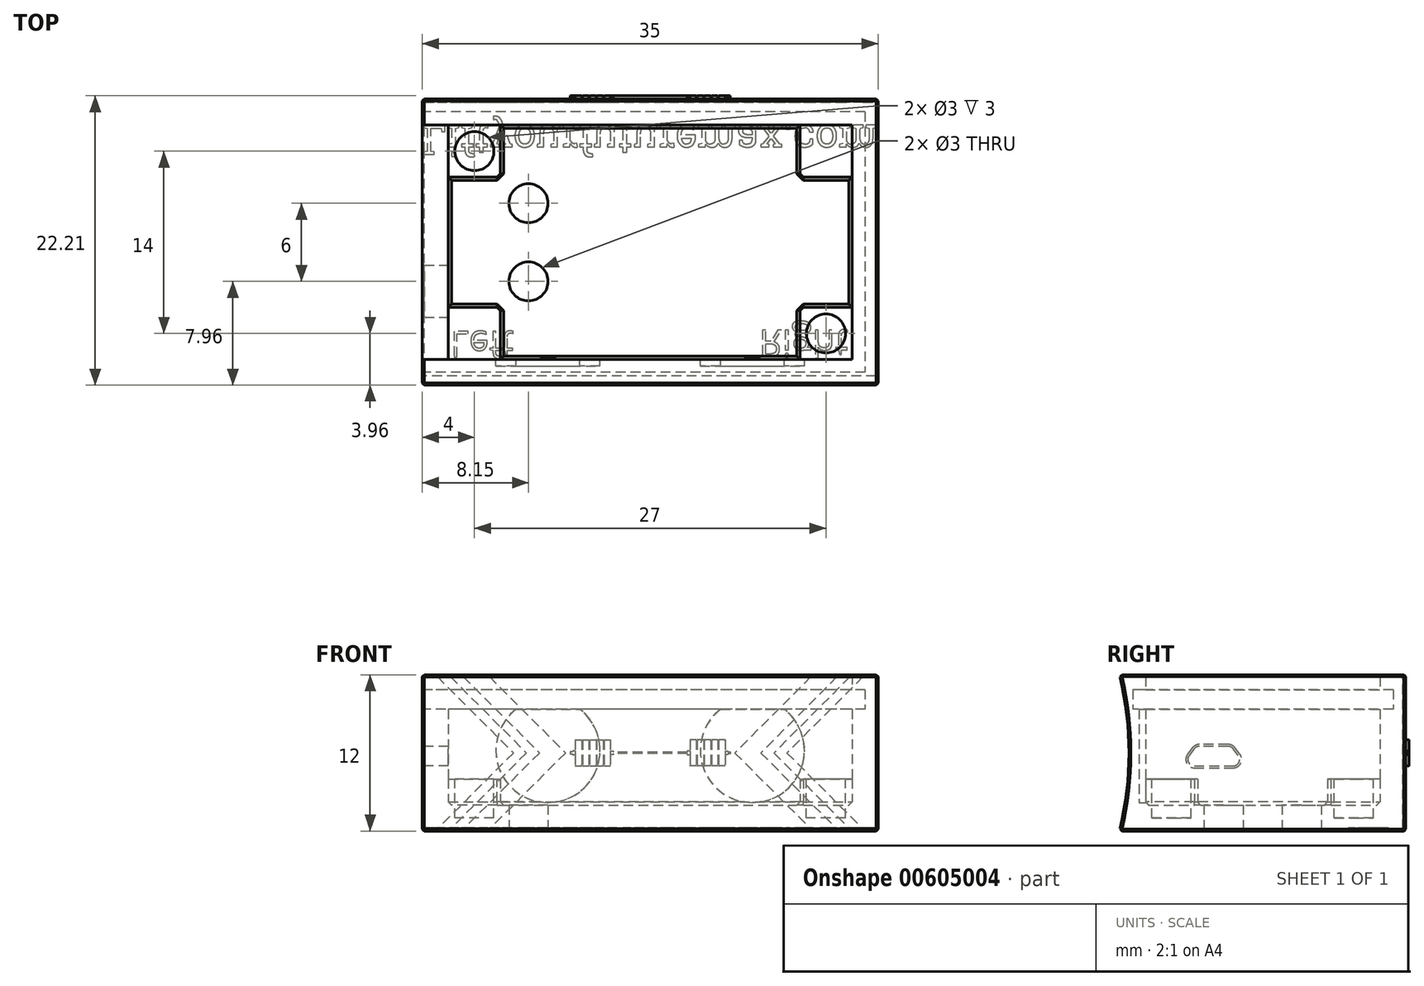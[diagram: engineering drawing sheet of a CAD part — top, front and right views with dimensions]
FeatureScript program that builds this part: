
annotation { "Feature Type Name" : "Feature", "Feature Type Description" : "" }
export const myFeature = defineFeature(function(context is Context, id is Id, definition is map)
    precondition{}
    {
        {
            var Q0;
            Q0=qCreatedBy(makeId("Top.planeOp"),FACE);
            var sketch = newSketch(context, id + "F0", { "sketchPlane" : qUnion([Q0])});
            skLineSegment(sketch, "E0.bottom", {"start": v(-17.5, 11) * mm, "end": v(17.5, 11) * mm});
            skLineSegment(sketch, "E0.top", {"start": v(-17.5, -11) * mm, "end": v(17.5, -11) * mm});
            skLineSegment(sketch, "E0.left", {"start": v(-17.5, 11) * mm, "end": v(-17.5, -11) * mm});
            skLineSegment(sketch, "E0.right", {"start": v(17.5, 11) * mm, "end": v(17.5, -11) * mm});
            skSolve(sketch);
        }
        {
            var Q0;
            Q0 = qSketchRegion(id + "F0", true);
            extrude(context, id + "F1", {"entities" : qUnion([Q0]), "depth" : 12 * mm, "offsetDistance" : 25 * mm});
        }
        {
            var Q0;
            Q0=makeQuery(id+"F1.opExtrude","CAP_FACE",FACE,{"disambiguationData":[OSD([sQuery(id+"F0.wireOp",EDGE,"E0.bottom"),sQuery(id+"F0.wireOp",EDGE,"E0.top"),sQuery(id+"F0.wireOp",EDGE,"E0.left"),sQuery(id+"F0.wireOp",EDGE,"E0.right")])],"isStart":false});
            shell(context, id + "F2", {"entities" : qUnion([Q0]), "thickness" : 2 * mm});
        }
        {
            var Q0;
            Q0=makeQuery(id+"F2.opShell","OFFSET_FACE",FACE,{"disambiguationData":[OSD([sQuery(id+"F0.wireOp",EDGE,"E0.bottom"),sQuery(id+"F0.wireOp",EDGE,"E0.top"),sQuery(id+"F0.wireOp",EDGE,"E0.left"),sQuery(id+"F0.wireOp",EDGE,"E0.right")])]});
            var sketch = newSketch(context, id + "F3", { "sketchPlane" : qUnion([Q0])});
            skLineSegment(sketch, "E1.bottom", {"start": v(-15.5, 9) * mm, "end": v(-11.5, 9) * mm});
            skLineSegment(sketch, "E1.top", {"start": v(-15.5, 5) * mm, "end": v(-11.5, 5) * mm});
            skLineSegment(sketch, "E1.left", {"start": v(-15.5, 9) * mm, "end": v(-15.5, 5) * mm});
            skLineSegment(sketch, "E1.right", {"start": v(-11.5, 9) * mm, "end": v(-11.5, 5) * mm});
            skLineSegment(sketch, "E2.bottom", {"start": v(15.5, 9) * mm, "end": v(11.5, 9) * mm});
            skLineSegment(sketch, "E2.top", {"start": v(15.5, 5) * mm, "end": v(11.5, 5) * mm});
            skLineSegment(sketch, "E2.left", {"start": v(15.5, 9) * mm, "end": v(15.5, 5) * mm});
            skLineSegment(sketch, "E2.right", {"start": v(11.5, 9) * mm, "end": v(11.5, 5) * mm});
            skLineSegment(sketch, "E3.bottom", {"start": v(15.5, -9) * mm, "end": v(11.5, -9) * mm});
            skLineSegment(sketch, "E3.top", {"start": v(15.5, -5) * mm, "end": v(11.5, -5) * mm});
            skLineSegment(sketch, "E3.left", {"start": v(15.5, -9) * mm, "end": v(15.5, -5) * mm});
            skLineSegment(sketch, "E3.right", {"start": v(11.5, -9) * mm, "end": v(11.5, -5) * mm});
            skLineSegment(sketch, "E4.bottom", {"start": v(-15.5, -9) * mm, "end": v(-11.5, -9) * mm});
            skLineSegment(sketch, "E4.top", {"start": v(-15.5, -5) * mm, "end": v(-11.5, -5) * mm});
            skLineSegment(sketch, "E4.left", {"start": v(-15.5, -9) * mm, "end": v(-15.5, -5) * mm});
            skLineSegment(sketch, "E4.right", {"start": v(-11.5, -9) * mm, "end": v(-11.5, -5) * mm});
            skSolve(sketch);
        }
        {
            var Q0;
            Q0 = qSketchRegion(id + "F3", true);
            extrude(context, id + "F4", {"entities" : qUnion([Q0]), "operationType" : NewBodyOperationType.ADD, "depth" : 2 * mm, "offsetDistance" : 25 * mm});
        }
        {
            var Q0;
            Q0=makeQuery(id+"F4.opExtrude","SWEPT_EDGE",EDGE,{"disambiguationData":[OSD([sQuery(id+"F3.wireOp",EDGE,"E1.top"),sQuery(id+"F3.wireOp",EDGE,"E1.right")])]});
            var Q1;
            {var subQ0=sQuery(id+"F0.wireOp",EDGE,"E0.bottom");Q1=makeQuery(id+"F2.opShell","OFFSET_EDGE",EDGE,{"disambiguationData":[OSD([subQ0]),TDD([makeQuery(id+"F1.opExtrude","CAP_EDGE",EDGE,{"disambiguationData":[OSD([subQ0])],"isStart":true})])]});}
            var Q2;
            {var subQ0=sQuery(id+"F0.wireOp",EDGE,"E0.left");Q2=makeQuery(id+"F2.opShell","OFFSET_EDGE",EDGE,{"disambiguationData":[OSD([subQ0]),TDD([makeQuery(id+"F1.opExtrude","CAP_EDGE",EDGE,{"disambiguationData":[OSD([subQ0])],"isStart":true})])]});}
            var Q3;
            Q3=makeQuery(id+"F2.opShell","OFFSET_FACE",FACE,{"disambiguationData":[OSD([sQuery(id+"F0.wireOp",EDGE,"E0.bottom"),sQuery(id+"F0.wireOp",EDGE,"E0.top"),sQuery(id+"F0.wireOp",EDGE,"E0.left"),sQuery(id+"F0.wireOp",EDGE,"E0.right")])]});
            var Q4;
            Q4=makeQuery(id+"F4.opExtrude","SWEPT_EDGE",EDGE,{"disambiguationData":[OSD([sQuery(id+"F3.wireOp",EDGE,"E2.top"),sQuery(id+"F3.wireOp",EDGE,"E2.right")])]});
            var Q5;
            Q5=makeQuery(id+"F4.opExtrude","SWEPT_EDGE",EDGE,{"disambiguationData":[OSD([sQuery(id+"F3.wireOp",EDGE,"E3.top"),sQuery(id+"F3.wireOp",EDGE,"E3.right")])]});
            var Q6;
            Q6=makeQuery(id+"F4.opExtrude","SWEPT_EDGE",EDGE,{"disambiguationData":[OSD([sQuery(id+"F3.wireOp",EDGE,"E4.top"),sQuery(id+"F3.wireOp",EDGE,"E4.right")])]});
            chamfer(context, id + "F5", {"entities" : qUnion([Q0, Q1, Q2, Q3, Q4, Q5, Q6]), "width" : 0.25 * mm, "tangentPropagation" : true});
        }
        {
            var Q0;
            Q0=makeQuery(id+"F4.opExtrude","CAP_FACE",FACE,{"disambiguationData":[OSD([sQuery(id+"F3.wireOp",EDGE,"E1.bottom"),sQuery(id+"F3.wireOp",EDGE,"E1.top"),sQuery(id+"F3.wireOp",EDGE,"E1.left"),sQuery(id+"F3.wireOp",EDGE,"E1.right")])],"isStart":false});
            var sketch = newSketch(context, id + "F6", { "sketchPlane" : qUnion([Q0])});
            skCircle(sketch, "E5", {"center": v(-13.5, 7) * mm, "radius": 1.5 * mm});
            skPoint(sketch, "E5.centerSnap0", {"position": v(-13.5, 5.88) * mm});
            skPoint(sketch, "E5.centerSnap1", {"position": v(-12.5, 7) * mm});
            skCircle(sketch, "E6.MirrorC", {"center": v(13.5, 7) * mm, "radius": 1.5 * mm});
            skCircle(sketch, "E7.MirrorC", {"center": v(-13.5, -7) * mm, "radius": 1.5 * mm});
            skCircle(sketch, "E8.MirrorC", {"center": v(13.5, -7) * mm, "radius": 1.5 * mm});
            skSolve(sketch);
        }
        {
            var Q0;
            Q0=makeQuery(id+"F6.imprint","IMPRINT",FACE,{"disambiguationData":[TD([[makeQuery(id+"F6.imprint","IMPRINT",EDGE,{"derivedFrom":sQuery(id+"F6.wireOp",EDGE,"E5")}),1.0]])]});
            var Q1;
            Q1=makeQuery(id+"F6.imprint","IMPRINT",FACE,{"disambiguationData":[TD([[makeQuery(id+"F6.imprint","IMPRINT",EDGE,{"derivedFrom":sQuery(id+"F6.wireOp",EDGE,"E6.MirrorC")}),-1.0]])]});
            var Q2;
            Q2=makeQuery(id+"F6.imprint","IMPRINT",FACE,{"disambiguationData":[TD([[makeQuery(id+"F6.imprint","IMPRINT",EDGE,{"derivedFrom":sQuery(id+"F6.wireOp",EDGE,"E8.MirrorC")}),1.0]])]});
            var Q3;
            Q3=makeQuery(id+"F6.imprint","IMPRINT",FACE,{"disambiguationData":[TD([[makeQuery(id+"F6.imprint","IMPRINT",EDGE,{"derivedFrom":sQuery(id+"F6.wireOp",EDGE,"E7.MirrorC")}),-1.0]])]});
            extrude(context, id + "F7", {"entities" : qUnion([Q0, Q1, Q2, Q3]), "operationType" : NewBodyOperationType.REMOVE, "oppositeDirection" : true, "depth" : 3 * mm, "offsetDistance" : 25 * mm});
        }
        {
            var Q0;
            Q0=makeQuery(id+"F1.opExtrude","SWEPT_FACE",FACE,{"disambiguationData":[OSD([sQuery(id+"F0.wireOp",EDGE,"E0.left")])]});
            var sketch = newSketch(context, id + "F8", { "sketchPlane" : qUnion([Q0])});
            skLineSegment(sketch, "E9", {"start": v(1.25, 5) * mm, "end": v(6.25, 5) * mm});
            skLineSegment(sketch, "E10", {"start": v(6.25, 5) * mm, "end": v(5.12, 6.5) * mm});
            skLineSegment(sketch, "E11", {"start": v(5.12, 6.5) * mm, "end": v(2.4, 6.5) * mm});
            skLineSegment(sketch, "E12", {"start": v(2.4, 6.5) * mm, "end": v(1.25, 5) * mm});
            skSolve(sketch);
        }
        {
            var Q0;
            Q0 = qSketchRegion(id + "F8", true);
            extrude(context, id + "F9", {"entities" : qUnion([Q0]), "operationType" : NewBodyOperationType.REMOVE, "oppositeDirection" : true, "depth" : 5 * mm, "offsetDistance" : 25 * mm});
        }
        {
            var Q0;
            Q0=makeQuery(id+"F9.boolean.opBoolean","COPY",EDGE,{"derivedFrom":makeQuery(id+"F9.opExtrude","SWEPT_EDGE",EDGE,{"disambiguationData":[OSD([sQuery(id+"F8.wireOp",EDGE,"E9"),sQuery(id+"F8.wireOp",EDGE,"E10")])]})});
            var Q1;
            Q1=makeQuery(id+"F9.boolean.opBoolean","COPY",EDGE,{"derivedFrom":makeQuery(id+"F9.opExtrude","SWEPT_EDGE",EDGE,{"disambiguationData":[OSD([sQuery(id+"F8.wireOp",EDGE,"E9"),sQuery(id+"F8.wireOp",EDGE,"E12")])]})});
            var Q2;
            Q2=makeQuery(id+"F9.boolean.opBoolean","COPY",EDGE,{"derivedFrom":makeQuery(id+"F9.opExtrude","SWEPT_EDGE",EDGE,{"disambiguationData":[OSD([sQuery(id+"F8.wireOp",EDGE,"E10"),sQuery(id+"F8.wireOp",EDGE,"E11")])]})});
            var Q3;
            Q3=makeQuery(id+"F9.boolean.opBoolean","COPY",EDGE,{"derivedFrom":makeQuery(id+"F9.opExtrude","SWEPT_EDGE",EDGE,{"disambiguationData":[OSD([sQuery(id+"F8.wireOp",EDGE,"E11"),sQuery(id+"F8.wireOp",EDGE,"E12")])]})});
            fillet(context, id + "F10", {"entities" : qUnion([Q0, Q1, Q2, Q3]), "radius" : 0.5 * mm, "tangentPropagation" : true, "allowEdgeOverflow" : false});
        }
        {
            var Q0;
            Q0=makeQuery(id+"F1.opExtrude","CAP_FACE",FACE,{"disambiguationData":[OSD([sQuery(id+"F0.wireOp",EDGE,"E0.bottom"),sQuery(id+"F0.wireOp",EDGE,"E0.top"),sQuery(id+"F0.wireOp",EDGE,"E0.left"),sQuery(id+"F0.wireOp",EDGE,"E0.right")])],"isStart":true});
            var sketch = newSketch(context, id + "F11", { "sketchPlane" : qUnion([Q0])});
            skText(sketch, "E13", { "text": "Liftyourfuturemax.com", "fontName": "RobotoSlab-Regular.ttf"});
            const initialGuessF11  = {"E13": [-0.0175, -0.009, 1, 0, 0.00228]};
            skSetInitialGuess(sketch, initialGuessF11);
            skSolve(sketch);
        }
        {
            var Q0;
            Q0 = qSketchRegion(id + "F11", true);
            extrude(context, id + "F12", {"entities" : qUnion([Q0]), "operationType" : NewBodyOperationType.REMOVE, "oppositeDirection" : true, "depth" : 0.25 * mm, "offsetDistance" : 25 * mm});
        }
        {
            var Q0;
            Q0=makeQuery(id+"F1.opExtrude","SWEPT_FACE",FACE,{"disambiguationData":[OSD([sQuery(id+"F0.wireOp",EDGE,"E0.left")])]});
            var sketch = newSketch(context, id + "F13", { "sketchPlane" : qUnion([Q0])});
            skArc(sketch, "E14", {"start": v(11, 12) * mm, "mid": v(10.27, 6) * mm, "end": v(11, 0) * mm});
            skSolve(sketch);
        }
        {
            var Q0;
            Q0=makeQuery(id+"F13.imprint","IMPRINT",FACE,{"disambiguationData":[TD([[makeQuery(id+"F13.imprint","IMPRINT",EDGE,{"derivedFrom":sQuery(id+"F13.wireOp",EDGE,"E14")}),1.0]])]});
            extrude(context, id + "F14", {"entities" : qUnion([Q0]), "operationType" : NewBodyOperationType.REMOVE, "oppositeDirection" : true, "depth" : 50 * mm, "offsetDistance" : 25 * mm});
        }
        {
            var Q0;
            Q0=makeQuery(id+"F1.opExtrude","SWEPT_FACE",FACE,{"disambiguationData":[OSD([sQuery(id+"F0.wireOp",EDGE,"E0.right")])]});
            var Q1;
            Q1=makeQuery(id+"F1.opExtrude","SWEPT_FACE",FACE,{"disambiguationData":[OSD([sQuery(id+"F0.wireOp",EDGE,"E0.bottom")])]});
            var Q2;
            Q2=makeQuery(id+"F1.opExtrude","SWEPT_FACE",FACE,{"disambiguationData":[OSD([sQuery(id+"F0.wireOp",EDGE,"E0.left")])]});
            var Q3;
            Q3=makeQuery(id+"F14.boolean.opBoolean","COPY",FACE,{"derivedFrom":makeQuery(id+"F14.opExtrude","SWEPT_FACE",FACE,{"disambiguationData":[OSD([sQuery(id+"F13.wireOp",EDGE,"E14")])]})});
            chamfer(context, id + "F15", {"entities" : qUnion([Q0, Q1, Q2, Q3]), "width" : 0.15 * mm, "tangentPropagation" : true});
        }
        {
            var Q0;
            Q0=qCreatedBy(makeId("Front.planeOp"),FACE);
            var sketch = newSketch(context, id + "F16", { "sketchPlane" : qUnion([Q0])});
            skCircle(sketch, "E15", {"center": v(7.85, 6.18) * mm, "radius": 4 * mm});
            skCircle(sketch, "E16", {"center": v(-7.85, 6.18) * mm, "radius": 4 * mm});
            skSolve(sketch);
        }
        {
            var Q0;
            Q0 = qSketchRegion(id + "F16", true);
            extrude(context, id + "F17", {"entities" : qUnion([Q0]), "operationType" : NewBodyOperationType.REMOVE, "depth" : 9.5 * mm, "offsetDistance" : 25 * mm});
        }
        {
            var Q0;
            {var subQ0=sQuery(id+"F0.wireOp",EDGE,"E0.right");var subQ1=sQuery(id+"F0.wireOp",EDGE,"E0.left");var subQ2=sQuery(id+"F0.wireOp",EDGE,"E0.top");var subQ3=sQuery(id+"F0.wireOp",EDGE,"E0.bottom");Q0=makeQuery(id+"F12.boolean.opBoolean","SPLIT",FACE,{"disambiguationData":[TD([makeQuery(id+"F1.opExtrude","SWEPT_FACE",FACE,{"disambiguationData":[OSD([subQ3])]})])],"derivedFrom":makeQuery(id+"F1.opExtrude","CAP_FACE",FACE,{"disambiguationData":[OSD([subQ3,subQ2,subQ1,subQ0])],"isStart":true})});}
            var sketch = newSketch(context, id + "F18", { "sketchPlane" : qUnion([Q0])});
            skText(sketch, "E17", { "text": "Left", "fontName": "OpenSans-Regular.ttf"});
            skText(sketch, "E18", { "text": "Right", "fontName": "OpenSans-Regular.ttf"});
            const initialGuessF18  = {"E17": [-0.01535, 0.00683, 1, 0, 0.00198], "E18": [0.00835, 0.00673, 1, 0, 0.00207]};
            skSetInitialGuess(sketch, initialGuessF18);
            skSolve(sketch);
        }
        {
            var Q0;
            Q0 = qSketchRegion(id + "F18", true);
            extrude(context, id + "F19", {"entities" : qUnion([Q0]), "operationType" : NewBodyOperationType.REMOVE, "oppositeDirection" : true, "depth" : 0.15 * mm, "offsetDistance" : 25 * mm});
        }
        {
            var Q0;
            Q0=makeQuery(id+"F1.opExtrude","SWEPT_FACE",FACE,{"disambiguationData":[OSD([sQuery(id+"F0.wireOp",EDGE,"E0.bottom")])]});
            var sketch = newSketch(context, id + "F20", { "sketchPlane" : qUnion([Q0])});
            skLineSegment(sketch, "E19", {"start": v(-16.35, 11.85) * mm, "end": v(-10.5, 6) * mm});
            skLineSegment(sketch, "E20", {"start": v(-10.5, 6) * mm, "end": v(-16.35, 0.15) * mm});
            skLineSegment(sketch, "E21", {"start": v(-15.35, 11.85) * mm, "end": v(-9.5, 6) * mm});
            skPoint(sketch, "E21.endSnap0", {"position": v(-17.35, 6) * mm});
            skLineSegment(sketch, "E22", {"start": v(-9.5, 6) * mm, "end": v(-15.35, 0.15) * mm});
            skLineSegment(sketch, "E23", {"start": v(-14.35, 11.85) * mm, "end": v(-8.5, 6) * mm});
            skLineSegment(sketch, "E24", {"start": v(-8.5, 6) * mm, "end": v(-14.35, 0.15) * mm});
            skLineSegment(sketch, "E25", {"start": v(-13.35, 11.85) * mm, "end": v(-7.5, 6) * mm});
            skLineSegment(sketch, "E26", {"start": v(-7.5, 6) * mm, "end": v(-13.35, 0.15) * mm});
            skLineSegment(sketch, "E27", {"start": v(-12.35, 11.85) * mm, "end": v(-6.5, 6) * mm});
            skLineSegment(sketch, "E28", {"start": v(-6.5, 6) * mm, "end": v(-12.35, 0.15) * mm});
            skLineSegment(sketch, "E29.MirrorCS", {"start": v(12.35, 11.85) * mm, "end": v(6.5, 6) * mm});
            skLineSegment(sketch, "E30.MirrorCS", {"start": v(13.35, 11.85) * mm, "end": v(7.5, 6) * mm});
            skLineSegment(sketch, "E31.MirrorCS", {"start": v(14.35, 11.85) * mm, "end": v(8.5, 6) * mm});
            skLineSegment(sketch, "E32.MirrorCS", {"start": v(15.35, 11.85) * mm, "end": v(9.5, 6) * mm});
            skLineSegment(sketch, "E33.MirrorCS", {"start": v(16.35, 11.85) * mm, "end": v(10.5, 6) * mm});
            skLineSegment(sketch, "E34.MirrorCS", {"start": v(6.5, 6) * mm, "end": v(12.35, 0.15) * mm});
            skLineSegment(sketch, "E35.MirrorCS", {"start": v(7.5, 6) * mm, "end": v(13.35, 0.15) * mm});
            skLineSegment(sketch, "E36.MirrorCS", {"start": v(8.5, 6) * mm, "end": v(14.35, 0.15) * mm});
            skLineSegment(sketch, "E37.MirrorCS", {"start": v(9.5, 6) * mm, "end": v(15.35, 0.15) * mm});
            skLineSegment(sketch, "E38.MirrorCS", {"start": v(10.5, 6) * mm, "end": v(16.35, 0.15) * mm});
            skSolve(sketch);
        }
        {
            var Q0;
            {var subQ3=sQuery(id+"F20.wireOp",EDGE,"E27");Q0=makeQuery(id+"F20.imprint","IMPRINT",FACE,{"disambiguationData":[TD([[makeQuery(id+"F20.imprint","IMPRINT",EDGE,{"derivedFrom":subQ3}),1.0]])]});}
            var Q1;
            {var subQ6=sQuery(id+"F20.wireOp",EDGE,"E19");Q1=makeQuery(id+"F20.imprint","IMPRINT",FACE,{"disambiguationData":[TD([[makeQuery(id+"F20.imprint","IMPRINT",EDGE,{"derivedFrom":subQ6}),-1.0]])]});}
            var Q2;
            {var subQ6=sQuery(id+"F20.wireOp",EDGE,"E33.MirrorCS");Q2=makeQuery(id+"F20.imprint","IMPRINT",FACE,{"disambiguationData":[TD([[makeQuery(id+"F20.imprint","IMPRINT",EDGE,{"derivedFrom":subQ6}),1.0]])]});}
            var Q3;
            {var subQ3=sQuery(id+"F20.wireOp",EDGE,"E21");Q3=makeQuery(id+"F20.imprint","IMPRINT",FACE,{"disambiguationData":[TD([[makeQuery(id+"F20.imprint","IMPRINT",EDGE,{"derivedFrom":subQ3}),1.0]])]});}
            var Q4;
            {var subQ3=sQuery(id+"F20.wireOp",EDGE,"E31.MirrorCS");Q4=makeQuery(id+"F20.imprint","IMPRINT",FACE,{"disambiguationData":[TD([[makeQuery(id+"F20.imprint","IMPRINT",EDGE,{"derivedFrom":subQ3}),1.0]])]});}
            extrude(context, id + "F21", {"entities" : qUnion([Q0, Q1, Q2, Q3, Q4]), "operationType" : NewBodyOperationType.REMOVE, "oppositeDirection" : true, "depth" : 0.25 * mm, "offsetDistance" : 25 * mm});
        }
        {
            var Q0;
            Q0=makeQuery(id+"F21.boolean.opBoolean","COPY",FACE,{"derivedFrom":makeQuery(id+"F21.opExtrude","CAP_FACE",FACE,{"disambiguationData":[OSD([sQuery(id+"F0.wireOp",EDGE,"E0.bottom"),sQuery(id+"F20.wireOp",EDGE,"E27"),sQuery(id+"F20.wireOp",EDGE,"E28"),sQuery(id+"F20.wireOp",EDGE,"E29.MirrorCS"),sQuery(id+"F20.wireOp",EDGE,"E34.MirrorCS")])],"isStart":false})});
            var sketch = newSketch(context, id + "F22", { "sketchPlane" : qUnion([Q0])});
            skLineSegment(sketch, "E39.bottom", {"start": v(-5.2, 7) * mm, "end": v(-4.7, 7) * mm});
            skLineSegment(sketch, "E39.top", {"start": v(-5.2, 5) * mm, "end": v(-4.7, 5) * mm});
            skLineSegment(sketch, "E39.left", {"start": v(-5.2, 7) * mm, "end": v(-5.2, 5) * mm});
            skLineSegment(sketch, "E39.right", {"start": v(-4.7, 7) * mm, "end": v(-4.7, 5) * mm});
            skLineSegment(sketch, "E40.bottom", {"start": v(-4.65, 7) * mm, "end": v(-4.15, 7) * mm});
            skLineSegment(sketch, "E40.top", {"start": v(-4.65, 5) * mm, "end": v(-4.15, 5) * mm});
            skLineSegment(sketch, "E40.left", {"start": v(-4.65, 7) * mm, "end": v(-4.65, 5) * mm});
            skLineSegment(sketch, "E40.right", {"start": v(-4.15, 7) * mm, "end": v(-4.15, 5) * mm});
            skLineSegment(sketch, "E41.bottom", {"start": v(-4.1, 7) * mm, "end": v(-3.6, 7) * mm});
            skLineSegment(sketch, "E41.top", {"start": v(-4.1, 5) * mm, "end": v(-3.6, 5) * mm});
            skLineSegment(sketch, "E41.left", {"start": v(-4.1, 7) * mm, "end": v(-4.1, 5) * mm});
            skLineSegment(sketch, "E41.right", {"start": v(-3.6, 7) * mm, "end": v(-3.6, 5) * mm});
            skLineSegment(sketch, "E42.bottom", {"start": v(-3.55, 7) * mm, "end": v(-3.05, 7) * mm});
            skLineSegment(sketch, "E42.top", {"start": v(-3.55, 5) * mm, "end": v(-3.05, 5) * mm});
            skLineSegment(sketch, "E42.left", {"start": v(-3.55, 7) * mm, "end": v(-3.55, 5) * mm});
            skLineSegment(sketch, "E42.right", {"start": v(-3.05, 7) * mm, "end": v(-3.05, 5) * mm});
            skLineSegment(sketch, "E43.bottom", {"start": v(-5.75, 7) * mm, "end": v(-5.25, 7) * mm});
            skLineSegment(sketch, "E43.top", {"start": v(-5.75, 5) * mm, "end": v(-5.25, 5) * mm});
            skLineSegment(sketch, "E43.left", {"start": v(-5.75, 7) * mm, "end": v(-5.75, 5) * mm});
            skLineSegment(sketch, "E43.right", {"start": v(-5.25, 7) * mm, "end": v(-5.25, 5) * mm});
            skLineSegment(sketch, "E44.MirrorCS", {"start": v(3.05, 7) * mm, "end": v(3.05, 5) * mm});
            skLineSegment(sketch, "E45.MirrorCS", {"start": v(3.55, 7) * mm, "end": v(3.55, 5) * mm});
            skLineSegment(sketch, "E46.MirrorCS", {"start": v(3.6, 7) * mm, "end": v(3.6, 5) * mm});
            skLineSegment(sketch, "E47.MirrorCS", {"start": v(4.1, 7) * mm, "end": v(4.1, 5) * mm});
            skLineSegment(sketch, "E48.MirrorCS", {"start": v(4.15, 7) * mm, "end": v(4.15, 5) * mm});
            skLineSegment(sketch, "E49.MirrorCS", {"start": v(4.65, 7) * mm, "end": v(4.65, 5) * mm});
            skLineSegment(sketch, "E50.MirrorCS", {"start": v(4.7, 7) * mm, "end": v(4.7, 5) * mm});
            skLineSegment(sketch, "E51.MirrorCS", {"start": v(5.2, 7) * mm, "end": v(5.2, 5) * mm});
            skLineSegment(sketch, "E52.MirrorCS", {"start": v(5.25, 7) * mm, "end": v(5.25, 5) * mm});
            skLineSegment(sketch, "E53.MirrorCS", {"start": v(5.75, 7) * mm, "end": v(5.75, 5) * mm});
            skLineSegment(sketch, "E54.MirrorCS", {"start": v(5.75, 7) * mm, "end": v(5.25, 7) * mm});
            skLineSegment(sketch, "E55.MirrorCS", {"start": v(5.2, 7) * mm, "end": v(4.7, 7) * mm});
            skLineSegment(sketch, "E56.MirrorCS", {"start": v(4.65, 7) * mm, "end": v(4.15, 7) * mm});
            skLineSegment(sketch, "E57.MirrorCS", {"start": v(4.1, 7) * mm, "end": v(3.6, 7) * mm});
            skLineSegment(sketch, "E58.MirrorCS", {"start": v(3.55, 7) * mm, "end": v(3.05, 7) * mm});
            skLineSegment(sketch, "E59.MirrorCS", {"start": v(3.55, 5) * mm, "end": v(3.05, 5) * mm});
            skLineSegment(sketch, "E60.MirrorCS", {"start": v(4.1, 5) * mm, "end": v(3.6, 5) * mm});
            skLineSegment(sketch, "E61.MirrorCS", {"start": v(4.65, 5) * mm, "end": v(4.15, 5) * mm});
            skLineSegment(sketch, "E62.MirrorCS", {"start": v(5.2, 5) * mm, "end": v(4.7, 5) * mm});
            skLineSegment(sketch, "E63.MirrorCS", {"start": v(5.75, 5) * mm, "end": v(5.25, 5) * mm});
            skLineSegment(sketch, "E64", {"start": v(-3.05, 6.15) * mm, "end": v(-2.85, 6.15) * mm});
            skLineSegment(sketch, "E65", {"start": v(-2.85, 6.15) * mm, "end": v(-2.85, 5.85) * mm});
            skLineSegment(sketch, "E66", {"start": v(-2.85, 5.85) * mm, "end": v(-3.05, 5.85) * mm});
            skLineSegment(sketch, "E67.MirrorCS", {"start": v(3.05, 6.15) * mm, "end": v(2.85, 6.15) * mm});
            skLineSegment(sketch, "E68.MirrorCS", {"start": v(2.85, 6.15) * mm, "end": v(2.85, 5.85) * mm});
            skLineSegment(sketch, "E69.MirrorCS", {"start": v(2.85, 5.85) * mm, "end": v(3.05, 5.85) * mm});
            skLineSegment(sketch, "E70", {"start": v(-2.85, 6.05) * mm, "end": v(2.85, 6.05) * mm});
            skLineSegment(sketch, "E71", {"start": v(-2.85, 5.95) * mm, "end": v(2.85, 5.95) * mm});
            skLineSegment(sketch, "E72", {"start": v(-5.75, 6.15) * mm, "end": v(-5.94, 6.15) * mm});
            skLineSegment(sketch, "E73", {"start": v(-5.94, 6.15) * mm, "end": v(-5.94, 6.08) * mm});
            skLineSegment(sketch, "E74", {"start": v(-5.94, 6.08) * mm, "end": v(-6.14, 6.08) * mm});
            skLineSegment(sketch, "E75", {"start": v(-6.14, 6.08) * mm, "end": v(-6.14, 5.93) * mm});
            skLineSegment(sketch, "E76", {"start": v(-6.14, 5.93) * mm, "end": v(-5.94, 5.93) * mm});
            skLineSegment(sketch, "E77", {"start": v(-5.94, 5.93) * mm, "end": v(-5.94, 5.85) * mm});
            skLineSegment(sketch, "E78", {"start": v(-5.94, 5.85) * mm, "end": v(-5.75, 5.85) * mm});
            skLineSegment(sketch, "E79.MirrorCS", {"start": v(5.75, 6.15) * mm, "end": v(5.94, 6.15) * mm});
            skLineSegment(sketch, "E80.MirrorCS", {"start": v(5.94, 6.15) * mm, "end": v(5.94, 6.08) * mm});
            skLineSegment(sketch, "E81.MirrorCS", {"start": v(5.94, 6.08) * mm, "end": v(6.14, 6.08) * mm});
            skLineSegment(sketch, "E82.MirrorCS", {"start": v(6.14, 6.08) * mm, "end": v(6.14, 5.93) * mm});
            skLineSegment(sketch, "E83.MirrorCS", {"start": v(6.14, 5.93) * mm, "end": v(5.94, 5.93) * mm});
            skLineSegment(sketch, "E84.MirrorCS", {"start": v(5.94, 5.93) * mm, "end": v(5.94, 5.85) * mm});
            skLineSegment(sketch, "E85.MirrorCS", {"start": v(5.94, 5.85) * mm, "end": v(5.75, 5.85) * mm});
            skSolve(sketch);
        }
        {
            var Q0;
            {var subQ0=sQuery(id+"F22.wireOp",EDGE,"E70");Q0=makeQuery(id+"F22.imprint","IMPRINT",FACE,{"disambiguationData":[TD([[makeQuery(id+"F22.imprint","IMPRINT",EDGE,{"derivedFrom":subQ0}),-1.0]])]});}
            var Q1;
            {var subQ3=sQuery(id+"F22.wireOp",EDGE,"E64");Q1=makeQuery(id+"F22.imprint","IMPRINT",FACE,{"disambiguationData":[TD([[makeQuery(id+"F22.imprint","IMPRINT",EDGE,{"derivedFrom":subQ3}),-1.0]])]});}
            var Q2;
            {var subQ1=sQuery(id+"F22.wireOp",EDGE,"E67.MirrorCS");Q2=makeQuery(id+"F22.imprint","IMPRINT",FACE,{"disambiguationData":[TD([[makeQuery(id+"F22.imprint","IMPRINT",EDGE,{"derivedFrom":subQ1}),1.0]])]});}
            var Q3;
            {var subQ0=sQuery(id+"F22.wireOp",EDGE,"E79.MirrorCS");Q3=makeQuery(id+"F22.imprint","IMPRINT",FACE,{"disambiguationData":[TD([[makeQuery(id+"F22.imprint","IMPRINT",EDGE,{"derivedFrom":subQ0}),-1.0]])]});}
            var Q4;
            {var subQ0=sQuery(id+"F22.wireOp",EDGE,"E72");Q4=makeQuery(id+"F22.imprint","IMPRINT",FACE,{"disambiguationData":[TD([[makeQuery(id+"F22.imprint","IMPRINT",EDGE,{"derivedFrom":subQ0}),1.0]])]});}
            extrude(context, id + "F23", {"entities" : qUnion([Q0, Q1, Q2, Q3, Q4]), "depth" : 0.5 * mm, "offsetDistance" : 25 * mm});
        }
        {
            var Q0;
            Q0=makeQuery(id+"F22.imprint","IMPRINT",FACE,{"disambiguationData":[TD([[makeQuery(id+"F22.imprint","IMPRINT",EDGE,{"derivedFrom":sQuery(id+"F22.wireOp",EDGE,"E52.MirrorCS")}),1.0]])]});
            var Q1;
            Q1=makeQuery(id+"F22.imprint","IMPRINT",FACE,{"disambiguationData":[TD([[makeQuery(id+"F22.imprint","IMPRINT",EDGE,{"derivedFrom":sQuery(id+"F22.wireOp",EDGE,"E50.MirrorCS")}),1.0]])]});
            var Q2;
            Q2=makeQuery(id+"F22.imprint","IMPRINT",FACE,{"disambiguationData":[TD([[makeQuery(id+"F22.imprint","IMPRINT",EDGE,{"derivedFrom":sQuery(id+"F22.wireOp",EDGE,"E48.MirrorCS")}),1.0]])]});
            var Q3;
            Q3=makeQuery(id+"F22.imprint","IMPRINT",FACE,{"disambiguationData":[TD([[makeQuery(id+"F22.imprint","IMPRINT",EDGE,{"derivedFrom":sQuery(id+"F22.wireOp",EDGE,"E46.MirrorCS")}),1.0]])]});
            var Q4;
            Q4=makeQuery(id+"F22.imprint","IMPRINT",FACE,{"disambiguationData":[TD([[makeQuery(id+"F22.imprint","IMPRINT",EDGE,{"derivedFrom":sQuery(id+"F22.wireOp",EDGE,"E45.MirrorCS")}),-1.0]])]});
            var Q5;
            {var subQ3=sQuery(id+"F22.wireOp",EDGE,"E43.bottom");Q5=makeQuery(id+"F22.imprint","IMPRINT",FACE,{"disambiguationData":[TD([[makeQuery(id+"F22.imprint","IMPRINT",EDGE,{"derivedFrom":subQ3}),-1.0]])]});}
            var Q6;
            Q6=makeQuery(id+"F22.imprint","IMPRINT",FACE,{"disambiguationData":[TD([[makeQuery(id+"F22.imprint","IMPRINT",EDGE,{"derivedFrom":sQuery(id+"F22.wireOp",EDGE,"E39.bottom")}),-1.0]])]});
            var Q7;
            Q7=makeQuery(id+"F22.imprint","IMPRINT",FACE,{"disambiguationData":[TD([[makeQuery(id+"F22.imprint","IMPRINT",EDGE,{"derivedFrom":sQuery(id+"F22.wireOp",EDGE,"E40.bottom")}),-1.0]])]});
            var Q8;
            Q8=makeQuery(id+"F22.imprint","IMPRINT",FACE,{"disambiguationData":[TD([[makeQuery(id+"F22.imprint","IMPRINT",EDGE,{"derivedFrom":sQuery(id+"F22.wireOp",EDGE,"E41.bottom")}),-1.0]])]});
            var Q9;
            {var subQ1=sQuery(id+"F22.wireOp",EDGE,"E42.bottom");Q9=makeQuery(id+"F22.imprint","IMPRINT",FACE,{"disambiguationData":[TD([[makeQuery(id+"F22.imprint","IMPRINT",EDGE,{"derivedFrom":subQ1}),-1.0]])]});}
            extrude(context, id + "F24", {"entities" : qUnion([Q0, Q1, Q2, Q3, Q4, Q5, Q6, Q7, Q8, Q9]), "depth" : 0.5 * mm, "offsetDistance" : 25 * mm});
        }
        {
            var Q0;
            Q0=makeQuery(id+"F24.opExtrude","CAP_FACE",FACE,{"disambiguationData":[OSD([sQuery(id+"F22.wireOp",EDGE,"E43.bottom"),sQuery(id+"F22.wireOp",EDGE,"E43.top"),sQuery(id+"F22.wireOp",EDGE,"E43.left"),sQuery(id+"F22.wireOp",EDGE,"E43.right")])],"isStart":false});
            var Q1;
            Q1=makeQuery(id+"F24.opExtrude","CAP_FACE",FACE,{"disambiguationData":[OSD([sQuery(id+"F22.wireOp",EDGE,"E39.bottom"),sQuery(id+"F22.wireOp",EDGE,"E39.top"),sQuery(id+"F22.wireOp",EDGE,"E39.left"),sQuery(id+"F22.wireOp",EDGE,"E39.right")])],"isStart":false});
            var Q2;
            Q2=makeQuery(id+"F24.opExtrude","CAP_FACE",FACE,{"disambiguationData":[OSD([sQuery(id+"F22.wireOp",EDGE,"E40.bottom"),sQuery(id+"F22.wireOp",EDGE,"E40.top"),sQuery(id+"F22.wireOp",EDGE,"E40.left"),sQuery(id+"F22.wireOp",EDGE,"E40.right")])],"isStart":false});
            var Q3;
            Q3=makeQuery(id+"F24.opExtrude","CAP_FACE",FACE,{"disambiguationData":[OSD([sQuery(id+"F22.wireOp",EDGE,"E41.bottom"),sQuery(id+"F22.wireOp",EDGE,"E41.top"),sQuery(id+"F22.wireOp",EDGE,"E41.left"),sQuery(id+"F22.wireOp",EDGE,"E41.right")])],"isStart":false});
            var Q4;
            Q4=makeQuery(id+"F24.opExtrude","CAP_FACE",FACE,{"disambiguationData":[OSD([sQuery(id+"F22.wireOp",EDGE,"E42.bottom"),sQuery(id+"F22.wireOp",EDGE,"E42.top"),sQuery(id+"F22.wireOp",EDGE,"E42.left"),sQuery(id+"F22.wireOp",EDGE,"E42.right")])],"isStart":false});
            var Q5;
            Q5=makeQuery(id+"F24.opExtrude","CAP_FACE",FACE,{"disambiguationData":[OSD([sQuery(id+"F22.wireOp",EDGE,"E44.MirrorCS"),sQuery(id+"F22.wireOp",EDGE,"E45.MirrorCS"),sQuery(id+"F22.wireOp",EDGE,"E58.MirrorCS"),sQuery(id+"F22.wireOp",EDGE,"E59.MirrorCS")])],"isStart":false});
            var Q6;
            Q6=makeQuery(id+"F24.opExtrude","CAP_FACE",FACE,{"disambiguationData":[OSD([sQuery(id+"F22.wireOp",EDGE,"E46.MirrorCS"),sQuery(id+"F22.wireOp",EDGE,"E47.MirrorCS"),sQuery(id+"F22.wireOp",EDGE,"E57.MirrorCS"),sQuery(id+"F22.wireOp",EDGE,"E60.MirrorCS")])],"isStart":false});
            var Q7;
            Q7=makeQuery(id+"F24.opExtrude","CAP_FACE",FACE,{"disambiguationData":[OSD([sQuery(id+"F22.wireOp",EDGE,"E48.MirrorCS"),sQuery(id+"F22.wireOp",EDGE,"E49.MirrorCS"),sQuery(id+"F22.wireOp",EDGE,"E56.MirrorCS"),sQuery(id+"F22.wireOp",EDGE,"E61.MirrorCS")])],"isStart":false});
            var Q8;
            Q8=makeQuery(id+"F24.opExtrude","CAP_FACE",FACE,{"disambiguationData":[OSD([sQuery(id+"F22.wireOp",EDGE,"E50.MirrorCS"),sQuery(id+"F22.wireOp",EDGE,"E51.MirrorCS"),sQuery(id+"F22.wireOp",EDGE,"E55.MirrorCS"),sQuery(id+"F22.wireOp",EDGE,"E62.MirrorCS")])],"isStart":false});
            var Q9;
            Q9=makeQuery(id+"F24.opExtrude","CAP_FACE",FACE,{"disambiguationData":[OSD([sQuery(id+"F22.wireOp",EDGE,"E52.MirrorCS"),sQuery(id+"F22.wireOp",EDGE,"E53.MirrorCS"),sQuery(id+"F22.wireOp",EDGE,"E54.MirrorCS"),sQuery(id+"F22.wireOp",EDGE,"E63.MirrorCS")])],"isStart":false});
            fillet(context, id + "F25", {"entities" : qUnion([Q0, Q1, Q2, Q3, Q4, Q5, Q6, Q7, Q8, Q9]), "radius" : 0.05 * mm, "tangentPropagation" : true, "allowEdgeOverflow" : false});
        }
        {
            var Q0;
            {var subQ261=makeQuery(id+"F12.opExtrude","SWEPT_FACE",FACE,{"disambiguationData":[OSD([sQuery(id+"F11.wireOp",EDGE,"E13.sketch_text.stroke-8")])]});var subQ442=sQuery(id+"F0.wireOp",EDGE,"E0.left");var subQ443=sQuery(id+"F0.wireOp",EDGE,"E0.bottom");var subQ444=sQuery(id+"F0.wireOp",EDGE,"E0.right");var subQ447=sQuery(id+"F0.wireOp",EDGE,"E0.top");Q0=makeQuery(id+"F19.boolean.opBoolean","SPLIT",FACE,{"disambiguationData":[TD([makeQuery(id+"F12.boolean.opBoolean","COPY",FACE,{"derivedFrom":subQ261})])],"derivedFrom":makeQuery(id+"F15.opChamfer","SPLIT",FACE,{"disambiguationData":[OD(1.0)],"derivedFrom":makeQuery(id+"F12.boolean.opBoolean","SPLIT",FACE,{"disambiguationData":[TD([makeQuery(id+"F1.opExtrude","SWEPT_FACE",FACE,{"disambiguationData":[OSD([subQ443])]})])],"derivedFrom":makeQuery(id+"F1.opExtrude","CAP_FACE",FACE,{"disambiguationData":[OSD([subQ443,subQ447,subQ442,subQ444])],"isStart":true})})})});}
            var sketch = newSketch(context, id + "F26", { "sketchPlane" : qUnion([Q0])});
            skCircle(sketch, "E86", {"center": v(-9.35, 3) * mm, "radius": 1.5 * mm});
            skCircle(sketch, "E87", {"center": v(-9.35, -3) * mm, "radius": 1.5 * mm});
            skSolve(sketch);
        }
        {
            var Q0;
            Q0 = qSketchRegion(id + "F26", true);
            extrude(context, id + "F27", {"entities" : qUnion([Q0]), "operationType" : NewBodyOperationType.REMOVE, "oppositeDirection" : true, "depth" : 25 * mm, "offsetDistance" : 25 * mm});
        }
        {
            var Q0;
            Q0=makeQuery(id+"F1.opExtrude","SWEPT_FACE",FACE,{"disambiguationData":[OSD([sQuery(id+"F0.wireOp",EDGE,"E0.left")])]});
            var sketch = newSketch(context, id + "F28", { "sketchPlane" : qUnion([Q0])});
            skLineSegment(sketch, "E88.bottom", {"start": v(-10.02, 10.85) * mm, "end": v(9.98, 10.85) * mm});
            skLineSegment(sketch, "E88.top", {"start": v(-10.02, 9.35) * mm, "end": v(9.98, 9.35) * mm});
            skLineSegment(sketch, "E88.left", {"start": v(-10.02, 10.85) * mm, "end": v(-10.02, 9.35) * mm});
            skLineSegment(sketch, "E88.right", {"start": v(9.98, 10.85) * mm, "end": v(9.98, 9.35) * mm});
            skSolve(sketch);
        }
        {
            var Q0;
            Q0 = qSketchRegion(id + "F28", true);
            extrude(context, id + "F29", {"entities" : qUnion([Q0]), "operationType" : NewBodyOperationType.REMOVE, "oppositeDirection" : true, "depth" : 34 * mm, "offsetDistance" : 25 * mm});
        }
        {
            var Q0;
            Q0=makeQuery(id+"F1.opExtrude","SWEPT_FACE",FACE,{"disambiguationData":[OSD([sQuery(id+"F0.wireOp",EDGE,"E0.left")])]});
            var sketch = newSketch(context, id + "F30", { "sketchPlane" : qUnion([Q0])});
            skLineSegment(sketch, "E89.bottom", {"start": v(-9, 12.86) * mm, "end": v(9, 12.86) * mm});
            skLineSegment(sketch, "E89.top", {"start": v(-9, 10.85) * mm, "end": v(9, 10.85) * mm});
            skLineSegment(sketch, "E89.left", {"start": v(-9, 12.86) * mm, "end": v(-9, 10.85) * mm});
            skLineSegment(sketch, "E89.right", {"start": v(9, 12.86) * mm, "end": v(9, 10.85) * mm});
            skSolve(sketch);
        }
        {
            var Q0;
            Q0 = qSketchRegion(id + "F30", true);
            extrude(context, id + "F31", {"entities" : qUnion([Q0]), "operationType" : NewBodyOperationType.REMOVE, "oppositeDirection" : true, "depth" : 32.9 * mm, "offsetDistance" : 25 * mm});
        }
    });
